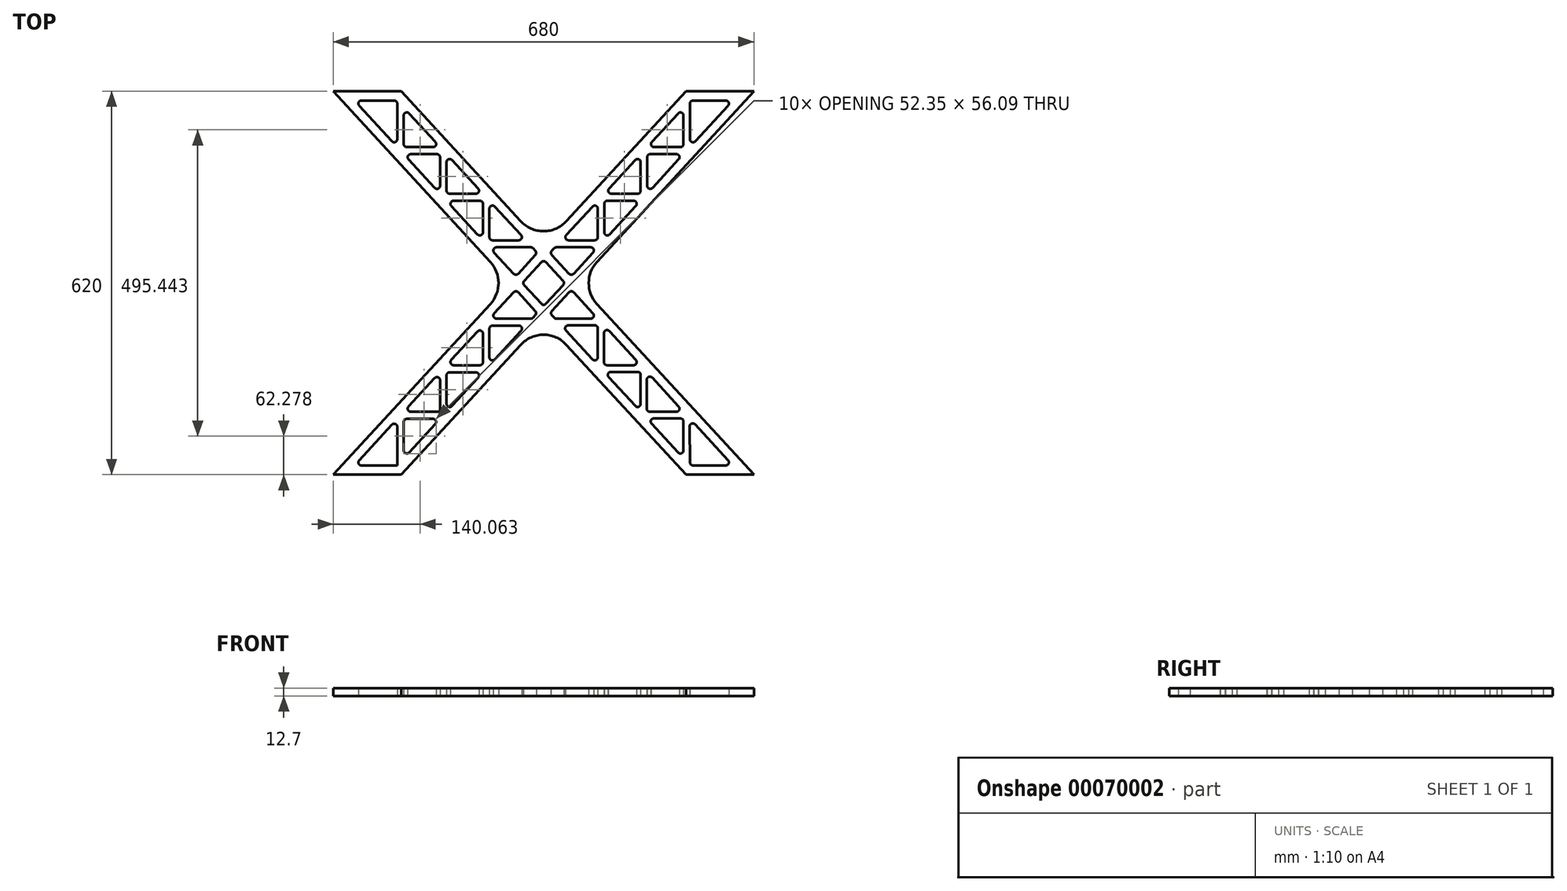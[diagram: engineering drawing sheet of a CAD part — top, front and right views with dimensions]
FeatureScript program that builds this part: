
annotation { "Feature Type Name" : "Feature", "Feature Type Description" : "" }
export const myFeature = defineFeature(function(context is Context, id is Id, definition is map)
    precondition{}
    {
        {
            var Q0;
            Q0=qCreatedBy(makeId("Top.planeOp"),FACE);
            var sketch = newSketch(context, id + "F0", { "sketchPlane" : qUnion([Q0])});
            skLineSegment(sketch, "E0.bottom", {"start": v(-340, 0) * mm, "end": v(-230, 0) * mm});
            skLineSegment(sketch, "E0.top", {"start": v(-340, 620) * mm, "end": v(-230, 620) * mm});
            skLineSegment(sketch, "E1", {"start": v(-230, 0) * mm, "end": v(-36.8, 210.14) * mm});
            skLineSegment(sketch, "E2", {"start": v(230, 620) * mm, "end": v(36.8, 409.86) * mm});
            skLineSegment(sketch, "E3", {"start": v(340, 0) * mm, "end": v(86.11, 276.16) * mm});
            skLineSegment(sketch, "E4", {"start": v(230, 0) * mm, "end": v(36.8, 210.14) * mm});
            skLineSegment(sketch, "E5.trimOffspring", {"start": v(230, 0) * mm, "end": v(340, 0) * mm});
            skLineSegment(sketch, "E6.trimOffspring", {"start": v(230, 620) * mm, "end": v(340, 620) * mm});
            skLineSegment(sketch, "E7.trimOffspring", {"start": v(-86.11, 343.84) * mm, "end": v(-340, 620) * mm});
            skLineSegment(sketch, "E8.trimOffspring", {"start": v(-86.11, 276.16) * mm, "end": v(-340, 0) * mm});
            skLineSegment(sketch, "E9.trimOffspring", {"start": v(-36.8, 409.86) * mm, "end": v(-230, 620) * mm});
            skLineSegment(sketch, "E10.trimOffspring", {"start": v(86.11, 343.84) * mm, "end": v(340, 620) * mm});
            skArc(sketch, "E11.filletArc", {"start": v(-36.8, 409.86) * mm, "mid": v(0, 393.7) * mm, "end": v(36.8, 409.86) * mm});
            skArc(sketch, "E12.filletArc", {"start": v(-86.11, 276.16) * mm, "mid": v(-72.92, 310) * mm, "end": v(-86.11, 343.84) * mm});
            skArc(sketch, "E13.filletArc", {"start": v(86.11, 343.84) * mm, "mid": v(72.92, 310) * mm, "end": v(86.11, 276.16) * mm});
            skArc(sketch, "E14.filletArc", {"start": v(36.8, 210.14) * mm, "mid": v(0, 226.3) * mm, "end": v(-36.8, 210.14) * mm});
            skLineSegment(sketch, "E15.0", {"start": v(-47.85, 399.7) * mm, "end": v(-78.93, 433.52) * mm});
            skLineSegment(sketch, "E15.1", {"start": v(-294.45, 605) * mm, "end": v(-241.59, 605) * mm});
            skLineSegment(sketch, "E15.2", {"start": v(-75.07, 354) * mm, "end": v(-79.9, 359.25) * mm});
            skLineSegment(sketch, "E15.4", {"start": v(-75.07, 266) * mm, "end": v(-79.9, 260.75) * mm});
            skLineSegment(sketch, "E15.6", {"start": v(75.07, 354) * mm, "end": v(79.9, 359.25) * mm});
            skLineSegment(sketch, "E15.7", {"start": v(241.59, 605) * mm, "end": v(294.45, 605) * mm});
            skLineSegment(sketch, "E15.8", {"start": v(217.43, 584.16) * mm, "end": v(175.04, 538.06) * mm});
            skLineSegment(sketch, "E15.9", {"start": v(298.13, 23.38) * mm, "end": v(244.76, 81.43) * mm});
            skLineSegment(sketch, "E15.10", {"start": v(241.55, 15) * mm, "end": v(294.45, 15) * mm});
            skLineSegment(sketch, "E15.11", {"start": v(217.43, 35.84) * mm, "end": v(174.44, 82.6) * mm});
            skLineSegment(sketch, "E15.13", {"start": v(-217.43, 35.84) * mm, "end": v(-175.04, 81.94) * mm});
            skLineSegment(sketch, "E15.15", {"start": v(-294.45, 15) * mm, "end": v(-236.59, 15) * mm});
            skLineSegment(sketch, "E16", {"start": v(-236.59, 15) * mm, "end": v(-236.59, 77.5) * mm});
            skLineSegment(sketch, "E17", {"start": v(-221.1, 90.32) * mm, "end": v(-178.73, 90.32) * mm});
            skLineSegment(sketch, "E18", {"start": v(-167.34, 101.72) * mm, "end": v(-167.34, 152.82) * mm});
            skLineSegment(sketch, "E19", {"start": v(-151.86, 165.65) * mm, "end": v(-109.48, 165.65) * mm});
            skLineSegment(sketch, "E20", {"start": v(-98.09, 182.04) * mm, "end": v(-98.09, 228.14) * mm});
            skLineSegment(sketch, "E21", {"start": v(-82.63, 241.02) * mm, "end": v(-40.07, 241.16) * mm});
            skLineSegment(sketch, "E22", {"start": v(97.48, 228.8) * mm, "end": v(97.48, 182.04) * mm});
            skLineSegment(sketch, "E23", {"start": v(108.87, 166.3) * mm, "end": v(151.86, 166.3) * mm});
            skLineSegment(sketch, "E24", {"start": v(166.73, 153.48) * mm, "end": v(166.73, 106.72) * mm});
            skLineSegment(sketch, "E25", {"start": v(178.12, 90.98) * mm, "end": v(221.1, 90.98) * mm});
            skLineSegment(sketch, "E26", {"start": v(236.08, 78) * mm, "end": v(236.55, 19.96) * mm});
            skLineSegment(sketch, "E27", {"start": v(-226.1, 39.22) * mm, "end": v(-226.1, 85.32) * mm});
            skLineSegment(sketch, "E28", {"start": v(-214.72, 101.72) * mm, "end": v(-167.34, 101.72) * mm});
            skLineSegment(sketch, "E29", {"start": v(-156.86, 114.54) * mm, "end": v(-156.86, 160.65) * mm});
            skLineSegment(sketch, "E30", {"start": v(-145.47, 177.04) * mm, "end": v(-103.09, 177.04) * mm});
            skLineSegment(sketch, "E31", {"start": v(-87.61, 189.87) * mm, "end": v(-87.61, 236.02) * mm});
            skLineSegment(sketch, "E32", {"start": v(-76.22, 252.36) * mm, "end": v(-20.56, 252.36) * mm});
            skLineSegment(sketch, "E33", {"start": v(87.61, 236.58) * mm, "end": v(87.61, 189.87) * mm});
            skLineSegment(sketch, "E34", {"start": v(102.48, 177.04) * mm, "end": v(145.47, 177.04) * mm});
            skLineSegment(sketch, "E35", {"start": v(156.86, 161.3) * mm, "end": v(156.86, 114.54) * mm});
            skLineSegment(sketch, "E36", {"start": v(171.73, 101.72) * mm, "end": v(214.5, 101.72) * mm});
            skLineSegment(sketch, "E37", {"start": v(226.1, 85.98) * mm, "end": v(226.1, 39.22) * mm});
            skLineSegment(sketch, "E38", {"start": v(-236.59, 600) * mm, "end": v(-236.59, 542.5) * mm});
            skLineSegment(sketch, "E39", {"start": v(-221.1, 529.68) * mm, "end": v(-178.73, 529.68) * mm});
            skLineSegment(sketch, "E40", {"start": v(-167.34, 513.28) * mm, "end": v(-167.34, 467.18) * mm});
            skLineSegment(sketch, "E41", {"start": v(-151.86, 454.35) * mm, "end": v(-109.48, 454.35) * mm});
            skLineSegment(sketch, "E42", {"start": v(-98.09, 437.96) * mm, "end": v(-98.09, 391.86) * mm});
            skLineSegment(sketch, "E43", {"start": v(-82.61, 379.03) * mm, "end": v(-40.23, 379.03) * mm});
            skLineSegment(sketch, "E44", {"start": v(98.09, 391.86) * mm, "end": v(98.09, 437.96) * mm});
            skLineSegment(sketch, "E45", {"start": v(109.48, 454.35) * mm, "end": v(151.86, 454.35) * mm});
            skLineSegment(sketch, "E46", {"start": v(167.34, 467.18) * mm, "end": v(167.34, 513.28) * mm});
            skLineSegment(sketch, "E47", {"start": v(178.73, 529.68) * mm, "end": v(221.1, 529.68) * mm});
            skLineSegment(sketch, "E48", {"start": v(236.59, 542.5) * mm, "end": v(236.59, 600) * mm});
            skLineSegment(sketch, "E49", {"start": v(226.1, 580.78) * mm, "end": v(226.1, 534.68) * mm});
            skLineSegment(sketch, "E50", {"start": v(214.72, 518.28) * mm, "end": v(172.34, 518.28) * mm});
            skLineSegment(sketch, "E51", {"start": v(156.86, 505.46) * mm, "end": v(156.86, 459.35) * mm});
            skLineSegment(sketch, "E52", {"start": v(145.47, 442.96) * mm, "end": v(103.09, 442.96) * mm});
            skLineSegment(sketch, "E53", {"start": v(87.61, 430.13) * mm, "end": v(87.61, 384.03) * mm});
            skLineSegment(sketch, "E54", {"start": v(76.22, 367.64) * mm, "end": v(20.56, 367.64) * mm});
            skLineSegment(sketch, "E55", {"start": v(-87.61, 384.03) * mm, "end": v(-87.61, 430.13) * mm});
            skLineSegment(sketch, "E56", {"start": v(-103.09, 442.96) * mm, "end": v(-145.47, 442.96) * mm});
            skLineSegment(sketch, "E57", {"start": v(-156.86, 459.35) * mm, "end": v(-156.86, 505.46) * mm});
            skLineSegment(sketch, "E58", {"start": v(-172.34, 518.28) * mm, "end": v(-214.72, 518.28) * mm});
            skLineSegment(sketch, "E59", {"start": v(-226.1, 534.68) * mm, "end": v(-226.1, 580.78) * mm});
            skLineSegment(sketch, "E60", {"start": v(47.85, 220.3) * mm, "end": v(36.12, 233.05) * mm});
            skLineSegment(sketch, "E61", {"start": v(-41.13, 294.91) * mm, "end": v(-13.3, 264.64) * mm});
            skLineSegment(sketch, "E62", {"start": v(75.07, 354) * mm, "end": v(48.5, 325.09) * mm});
            skLineSegment(sketch, "E63", {"start": v(-75.07, 266) * mm, "end": v(-48.5, 294.91) * mm});
            skLineSegment(sketch, "E64", {"start": v(75.07, 266) * mm, "end": v(48.5, 294.91) * mm});
            skLineSegment(sketch, "E65.trimOffspring", {"start": v(-245.27, 539.12) * mm, "end": v(-298.13, 596.62) * mm});
            skLineSegment(sketch, "E66.trimOffspring", {"start": v(-175.04, 538.06) * mm, "end": v(-217.43, 584.16) * mm});
            skLineSegment(sketch, "E67.trimOffspring", {"start": v(-176.02, 463.8) * mm, "end": v(-218.4, 509.9) * mm});
            skLineSegment(sketch, "E68.trimOffspring", {"start": v(-105.8, 462.74) * mm, "end": v(-148.18, 508.84) * mm});
            skLineSegment(sketch, "E69.trimOffspring", {"start": v(-106.77, 388.47) * mm, "end": v(-149.15, 434.58) * mm});
            skLineSegment(sketch, "E70.trimOffspring", {"start": v(-31.51, 313.38) * mm, "end": v(-3.68, 343.66) * mm});
            skLineSegment(sketch, "E71.trimOffspring", {"start": v(-48.5, 325.09) * mm, "end": v(-75.07, 354) * mm});
            skLineSegment(sketch, "E72.trimOffspring", {"start": v(40.23, 379.03) * mm, "end": v(82.61, 379.03) * mm});
            skLineSegment(sketch, "E73.trimOffspring", {"start": v(13.3, 355.36) * mm, "end": v(41.13, 325.09) * mm});
            skLineSegment(sketch, "E74.trimOffspring", {"start": v(-13.3, 362.13) * mm, "end": v(-16.88, 366.02) * mm});
            skLineSegment(sketch, "E75.trimOffspring", {"start": v(-20.56, 367.64) * mm, "end": v(-76.22, 367.64) * mm});
            skLineSegment(sketch, "E76.trimOffspring", {"start": v(-13.3, 355.36) * mm, "end": v(-41.13, 325.09) * mm});
            skLineSegment(sketch, "E77.trimOffspring", {"start": v(-36.55, 387.42) * mm, "end": v(-47.85, 399.7) * mm});
            skLineSegment(sketch, "E78.trimOffspring", {"start": v(36.55, 387.42) * mm, "end": v(47.85, 399.7) * mm});
            skLineSegment(sketch, "E79.trimOffspring", {"start": v(78.93, 433.52) * mm, "end": v(47.85, 399.7) * mm});
            skLineSegment(sketch, "E80.trimOffspring", {"start": v(176.02, 463.8) * mm, "end": v(218.4, 509.9) * mm});
            skLineSegment(sketch, "E81.trimOffspring", {"start": v(148.18, 508.84) * mm, "end": v(105.8, 462.74) * mm});
            skLineSegment(sketch, "E82.trimOffspring", {"start": v(245.27, 539.12) * mm, "end": v(298.13, 596.62) * mm});
            skLineSegment(sketch, "E83.trimOffspring", {"start": v(106.77, 388.47) * mm, "end": v(149.15, 434.58) * mm});
            skLineSegment(sketch, "E84.trimOffspring", {"start": v(13.3, 362.13) * mm, "end": v(16.88, 366.02) * mm});
            skLineSegment(sketch, "E85.trimOffspring", {"start": v(31.51, 306.62) * mm, "end": v(3.68, 276.34) * mm});
            skLineSegment(sketch, "E86.trimOffspring", {"start": v(31.51, 313.38) * mm, "end": v(3.68, 343.66) * mm});
            skLineSegment(sketch, "E87.trimOffspring", {"start": v(-13.3, 257.87) * mm, "end": v(-16.88, 253.98) * mm});
            skLineSegment(sketch, "E88.trimOffspring", {"start": v(-3.68, 276.34) * mm, "end": v(-31.51, 306.62) * mm});
            skLineSegment(sketch, "E89.trimOffspring", {"start": v(13.3, 264.64) * mm, "end": v(41.13, 294.91) * mm});
            skLineSegment(sketch, "E90.trimOffspring", {"start": v(20.56, 252.36) * mm, "end": v(76.22, 252.36) * mm});
            skLineSegment(sketch, "E91.trimOffspring", {"start": v(39.79, 241.43) * mm, "end": v(82.6, 241.58) * mm});
            skLineSegment(sketch, "E92.trimOffspring", {"start": v(16.88, 253.98) * mm, "end": v(13.3, 257.87) * mm});
            skLineSegment(sketch, "E93.trimOffspring", {"start": v(79.9, 260.75) * mm, "end": v(75.07, 266) * mm});
            skLineSegment(sketch, "E94.trimOffspring", {"start": v(78.93, 186.48) * mm, "end": v(47.85, 220.3) * mm});
            skLineSegment(sketch, "E95.trimOffspring", {"start": v(-36.37, 232.78) * mm, "end": v(-47.85, 220.3) * mm});
            skLineSegment(sketch, "E96.trimOffspring", {"start": v(-106.77, 231.53) * mm, "end": v(-149.15, 185.42) * mm});
            skLineSegment(sketch, "E97.trimOffspring", {"start": v(-78.93, 186.48) * mm, "end": v(-47.85, 220.3) * mm});
            skLineSegment(sketch, "E98.trimOffspring", {"start": v(-176.02, 156.2) * mm, "end": v(-218.4, 110.1) * mm});
            skLineSegment(sketch, "E99.trimOffspring", {"start": v(-148.18, 111.16) * mm, "end": v(-105.8, 157.26) * mm});
            skLineSegment(sketch, "E100.trimOffspring", {"start": v(-245.27, 80.88) * mm, "end": v(-298.13, 23.38) * mm});
            skLineSegment(sketch, "E101.trimOffspring", {"start": v(218.25, 110.27) * mm, "end": v(175.41, 156.86) * mm});
            skLineSegment(sketch, "E102.trimOffspring", {"start": v(148.18, 111.16) * mm, "end": v(105.2, 157.92) * mm});
            skLineSegment(sketch, "E103.trimOffspring", {"start": v(149.15, 185.42) * mm, "end": v(106.16, 232.18) * mm});
            skPoint(sketch, "E104.visualSharp", {"position": v(-305.83, 605) * mm});
            skArc(sketch, "E104.filletArc", {"start": v(-294.45, 605) * mm, "mid": v(-299.02, 602) * mm, "end": v(-298.13, 596.62) * mm});
            skPoint(sketch, "E105.visualSharp", {"position": v(-236.59, 605) * mm});
            skArc(sketch, "E105.filletArc", {"start": v(-236.59, 600) * mm, "mid": v(-238.05, 603.54) * mm, "end": v(-241.59, 605) * mm});
            skPoint(sketch, "E106.visualSharp", {"position": v(-236.59, 529.68) * mm});
            skArc(sketch, "E106.filletArc", {"start": v(-245.27, 539.12) * mm, "mid": v(-239.77, 537.84) * mm, "end": v(-236.59, 542.5) * mm});
            skPoint(sketch, "E107.visualSharp", {"position": v(-226.1, 593.6) * mm});
            skArc(sketch, "E107.filletArc", {"start": v(-217.43, 584.16) * mm, "mid": v(-222.93, 585.44) * mm, "end": v(-226.1, 580.78) * mm});
            skPoint(sketch, "E108.visualSharp", {"position": v(-167.34, 529.68) * mm});
            skArc(sketch, "E108.filletArc", {"start": v(-178.73, 529.68) * mm, "mid": v(-174.15, 532.67) * mm, "end": v(-175.04, 538.06) * mm});
            skPoint(sketch, "E109.visualSharp", {"position": v(-226.1, 529.68) * mm});
            skArc(sketch, "E109.filletArc", {"start": v(-226.1, 534.68) * mm, "mid": v(-224.65, 531.14) * mm, "end": v(-221.1, 529.68) * mm});
            skPoint(sketch, "E110.visualSharp", {"position": v(-156.86, 518.28) * mm});
            skArc(sketch, "E110.filletArc", {"start": v(-148.18, 508.84) * mm, "mid": v(-153.68, 510.11) * mm, "end": v(-156.86, 505.46) * mm});
            skPoint(sketch, "E111.visualSharp", {"position": v(-98.09, 454.35) * mm});
            skArc(sketch, "E111.filletArc", {"start": v(-109.48, 454.35) * mm, "mid": v(-104.9, 457.34) * mm, "end": v(-105.8, 462.74) * mm});
            skPoint(sketch, "E112.visualSharp", {"position": v(-156.86, 454.35) * mm});
            skArc(sketch, "E112.filletArc", {"start": v(-156.86, 459.35) * mm, "mid": v(-155.4, 455.82) * mm, "end": v(-151.86, 454.35) * mm});
            skPoint(sketch, "E113.visualSharp", {"position": v(-167.34, 454.35) * mm});
            skArc(sketch, "E113.filletArc", {"start": v(-176.02, 463.8) * mm, "mid": v(-170.52, 462.52) * mm, "end": v(-167.34, 467.18) * mm});
            skPoint(sketch, "E114.visualSharp", {"position": v(-167.34, 518.28) * mm});
            skArc(sketch, "E114.filletArc", {"start": v(-167.34, 513.28) * mm, "mid": v(-168.8, 516.82) * mm, "end": v(-172.34, 518.28) * mm});
            skPoint(sketch, "E115.visualSharp", {"position": v(-226.1, 518.28) * mm});
            skArc(sketch, "E115.filletArc", {"start": v(-214.72, 518.28) * mm, "mid": v(-219.3, 515.3) * mm, "end": v(-218.4, 509.9) * mm});
            skPoint(sketch, "E116.visualSharp", {"position": v(-98.09, 442.96) * mm});
            skArc(sketch, "E116.filletArc", {"start": v(-98.09, 437.96) * mm, "mid": v(-99.55, 441.5) * mm, "end": v(-103.09, 442.96) * mm});
            skPoint(sketch, "E117.visualSharp", {"position": v(-98.09, 379.03) * mm});
            skArc(sketch, "E117.filletArc", {"start": v(-106.77, 388.47) * mm, "mid": v(-101.27, 387.2) * mm, "end": v(-98.09, 391.86) * mm});
            skPoint(sketch, "E118.visualSharp", {"position": v(-156.86, 442.96) * mm});
            skArc(sketch, "E118.filletArc", {"start": v(-145.47, 442.96) * mm, "mid": v(-150.05, 439.97) * mm, "end": v(-149.15, 434.58) * mm});
            skPoint(sketch, "E119.visualSharp", {"position": v(-87.61, 442.96) * mm});
            skArc(sketch, "E119.filletArc", {"start": v(-78.93, 433.52) * mm, "mid": v(-84.43, 434.8) * mm, "end": v(-87.61, 430.13) * mm});
            skPoint(sketch, "E120.visualSharp", {"position": v(-28.84, 379.03) * mm});
            skArc(sketch, "E120.filletArc", {"start": v(-40.23, 379.03) * mm, "mid": v(-35.65, 382.02) * mm, "end": v(-36.55, 387.42) * mm});
            skPoint(sketch, "E121.visualSharp", {"position": v(-87.61, 379.03) * mm});
            skArc(sketch, "E121.filletArc", {"start": v(-87.61, 384.03) * mm, "mid": v(-86.15, 380.5) * mm, "end": v(-82.61, 379.03) * mm});
            skPoint(sketch, "E122.visualSharp", {"position": v(28.84, 379.03) * mm});
            skArc(sketch, "E122.filletArc", {"start": v(36.55, 387.42) * mm, "mid": v(35.65, 382.02) * mm, "end": v(40.23, 379.03) * mm});
            skPoint(sketch, "E123.visualSharp", {"position": v(87.61, 379.03) * mm});
            skArc(sketch, "E123.filletArc", {"start": v(82.61, 379.03) * mm, "mid": v(86.15, 380.5) * mm, "end": v(87.61, 384.03) * mm});
            skPoint(sketch, "E124.visualSharp", {"position": v(87.61, 442.96) * mm});
            skArc(sketch, "E124.filletArc", {"start": v(87.61, 430.13) * mm, "mid": v(84.43, 434.8) * mm, "end": v(78.93, 433.52) * mm});
            skPoint(sketch, "E125.visualSharp", {"position": v(98.09, 442.96) * mm});
            skArc(sketch, "E125.filletArc", {"start": v(103.09, 442.96) * mm, "mid": v(99.55, 441.5) * mm, "end": v(98.09, 437.96) * mm});
            skPoint(sketch, "E126.visualSharp", {"position": v(98.09, 379.03) * mm});
            skArc(sketch, "E126.filletArc", {"start": v(98.09, 391.86) * mm, "mid": v(101.27, 387.2) * mm, "end": v(106.77, 388.47) * mm});
            skPoint(sketch, "E127.visualSharp", {"position": v(156.86, 442.96) * mm});
            skArc(sketch, "E127.filletArc", {"start": v(149.15, 434.58) * mm, "mid": v(150.05, 439.97) * mm, "end": v(145.47, 442.96) * mm});
            skPoint(sketch, "E128.visualSharp", {"position": v(167.34, 454.35) * mm});
            skArc(sketch, "E128.filletArc", {"start": v(167.34, 467.18) * mm, "mid": v(170.52, 462.52) * mm, "end": v(176.02, 463.8) * mm});
            skPoint(sketch, "E129.visualSharp", {"position": v(226.1, 518.28) * mm});
            skArc(sketch, "E129.filletArc", {"start": v(218.4, 509.9) * mm, "mid": v(219.3, 515.3) * mm, "end": v(214.72, 518.28) * mm});
            skPoint(sketch, "E130.visualSharp", {"position": v(167.34, 518.28) * mm});
            skArc(sketch, "E130.filletArc", {"start": v(172.34, 518.28) * mm, "mid": v(168.8, 516.82) * mm, "end": v(167.34, 513.28) * mm});
            skPoint(sketch, "E131.visualSharp", {"position": v(156.86, 518.28) * mm});
            skArc(sketch, "E131.filletArc", {"start": v(156.86, 505.46) * mm, "mid": v(153.68, 510.11) * mm, "end": v(148.18, 508.84) * mm});
            skPoint(sketch, "E132.visualSharp", {"position": v(156.86, 454.35) * mm});
            skArc(sketch, "E132.filletArc", {"start": v(151.86, 454.35) * mm, "mid": v(155.4, 455.82) * mm, "end": v(156.86, 459.35) * mm});
            skPoint(sketch, "E133.visualSharp", {"position": v(98.09, 454.35) * mm});
            skArc(sketch, "E133.filletArc", {"start": v(105.8, 462.74) * mm, "mid": v(104.9, 457.34) * mm, "end": v(109.48, 454.35) * mm});
            skPoint(sketch, "E134.visualSharp", {"position": v(167.34, 529.68) * mm});
            skArc(sketch, "E134.filletArc", {"start": v(175.04, 538.06) * mm, "mid": v(174.15, 532.67) * mm, "end": v(178.73, 529.68) * mm});
            skPoint(sketch, "E135.visualSharp", {"position": v(226.1, 529.68) * mm});
            skArc(sketch, "E135.filletArc", {"start": v(221.1, 529.68) * mm, "mid": v(224.65, 531.14) * mm, "end": v(226.1, 534.68) * mm});
            skPoint(sketch, "E136.visualSharp", {"position": v(226.1, 593.6) * mm});
            skArc(sketch, "E136.filletArc", {"start": v(226.1, 580.78) * mm, "mid": v(222.93, 585.44) * mm, "end": v(217.43, 584.16) * mm});
            skPoint(sketch, "E137.visualSharp", {"position": v(236.59, 605) * mm});
            skArc(sketch, "E137.filletArc", {"start": v(241.59, 605) * mm, "mid": v(238.05, 603.54) * mm, "end": v(236.59, 600) * mm});
            skPoint(sketch, "E138.visualSharp", {"position": v(236.59, 529.68) * mm});
            skArc(sketch, "E138.filletArc", {"start": v(236.59, 542.5) * mm, "mid": v(239.77, 537.84) * mm, "end": v(245.27, 539.12) * mm});
            skPoint(sketch, "E139.visualSharp", {"position": v(305.83, 605) * mm});
            skArc(sketch, "E139.filletArc", {"start": v(298.13, 596.62) * mm, "mid": v(299.02, 602) * mm, "end": v(294.45, 605) * mm});
            skPoint(sketch, "E140.visualSharp", {"position": v(18.36, 367.64) * mm});
            skArc(sketch, "E140.filletArc", {"start": v(20.56, 367.64) * mm, "mid": v(18.55, 367.21) * mm, "end": v(16.88, 366.02) * mm});
            skPoint(sketch, "E141.visualSharp", {"position": v(10.19, 358.74) * mm});
            skArc(sketch, "E141.filletArc", {"start": v(13.3, 362.13) * mm, "mid": v(11.98, 358.74) * mm, "end": v(13.3, 355.36) * mm});
            skPoint(sketch, "E142.visualSharp", {"position": v(44.81, 321.08) * mm});
            skArc(sketch, "E142.filletArc", {"start": v(41.13, 325.09) * mm, "mid": v(44.81, 323.47) * mm, "end": v(48.5, 325.09) * mm});
            skPoint(sketch, "E143.visualSharp", {"position": v(87.61, 367.64) * mm});
            skArc(sketch, "E143.filletArc", {"start": v(79.9, 359.25) * mm, "mid": v(80.8, 364.65) * mm, "end": v(76.22, 367.64) * mm});
            skPoint(sketch, "E144.visualSharp", {"position": v(-10.19, 358.74) * mm});
            skArc(sketch, "E144.filletArc", {"start": v(-13.3, 355.36) * mm, "mid": v(-11.98, 358.74) * mm, "end": v(-13.3, 362.13) * mm});
            skPoint(sketch, "E145.visualSharp", {"position": v(-18.36, 367.64) * mm});
            skArc(sketch, "E145.filletArc", {"start": v(-16.88, 366.02) * mm, "mid": v(-18.55, 367.21) * mm, "end": v(-20.56, 367.64) * mm});
            skPoint(sketch, "E146.visualSharp", {"position": v(-44.81, 321.08) * mm});
            skArc(sketch, "E146.filletArc", {"start": v(-48.5, 325.09) * mm, "mid": v(-44.81, 323.47) * mm, "end": v(-41.13, 325.09) * mm});
            skPoint(sketch, "E147.visualSharp", {"position": v(-87.61, 367.64) * mm});
            skArc(sketch, "E147.filletArc", {"start": v(-76.22, 367.64) * mm, "mid": v(-80.8, 364.65) * mm, "end": v(-79.9, 359.25) * mm});
            skPoint(sketch, "E148.visualSharp", {"position": v(0, 347.66) * mm});
            skArc(sketch, "E148.filletArc", {"start": v(3.68, 343.66) * mm, "mid": v(0, 345.27) * mm, "end": v(-3.68, 343.66) * mm});
            skPoint(sketch, "E149.visualSharp", {"position": v(-34.62, 310) * mm});
            skArc(sketch, "E149.filletArc", {"start": v(-31.51, 313.38) * mm, "mid": v(-32.83, 310) * mm, "end": v(-31.51, 306.62) * mm});
            skPoint(sketch, "E150.visualSharp", {"position": v(34.62, 310) * mm});
            skArc(sketch, "E150.filletArc", {"start": v(31.51, 306.62) * mm, "mid": v(32.83, 310) * mm, "end": v(31.51, 313.38) * mm});
            skPoint(sketch, "E151.visualSharp", {"position": v(0, 272.34) * mm});
            skArc(sketch, "E151.filletArc", {"start": v(-3.68, 276.34) * mm, "mid": v(0, 274.73) * mm, "end": v(3.68, 276.34) * mm});
            skPoint(sketch, "E152.visualSharp", {"position": v(-10.19, 261.26) * mm});
            skArc(sketch, "E152.filletArc", {"start": v(-13.3, 257.87) * mm, "mid": v(-11.98, 261.26) * mm, "end": v(-13.3, 264.64) * mm});
            skPoint(sketch, "E153.visualSharp", {"position": v(-44.81, 298.92) * mm});
            skArc(sketch, "E153.filletArc", {"start": v(-41.13, 294.91) * mm, "mid": v(-44.81, 296.53) * mm, "end": v(-48.5, 294.91) * mm});
            skPoint(sketch, "E154.visualSharp", {"position": v(-87.61, 252.36) * mm});
            skArc(sketch, "E154.filletArc", {"start": v(-79.9, 260.75) * mm, "mid": v(-80.8, 255.35) * mm, "end": v(-76.22, 252.36) * mm});
            skPoint(sketch, "E155.visualSharp", {"position": v(-87.61, 241) * mm});
            skArc(sketch, "E155.filletArc", {"start": v(-82.63, 241.02) * mm, "mid": v(-86.15, 239.55) * mm, "end": v(-87.61, 236.02) * mm});
            skPoint(sketch, "E156.visualSharp", {"position": v(-28.63, 241.2) * mm});
            skArc(sketch, "E156.filletArc", {"start": v(-36.37, 232.78) * mm, "mid": v(-35.47, 238.18) * mm, "end": v(-40.07, 241.16) * mm});
            skPoint(sketch, "E157.visualSharp", {"position": v(-87.61, 177.04) * mm});
            skArc(sketch, "E157.filletArc", {"start": v(-87.61, 189.87) * mm, "mid": v(-84.43, 185.2) * mm, "end": v(-78.93, 186.48) * mm});
            skPoint(sketch, "E158.visualSharp", {"position": v(-98.09, 177.04) * mm});
            skArc(sketch, "E158.filletArc", {"start": v(-103.09, 177.04) * mm, "mid": v(-99.55, 178.5) * mm, "end": v(-98.09, 182.04) * mm});
            skPoint(sketch, "E159.visualSharp", {"position": v(-98.09, 240.97) * mm});
            skArc(sketch, "E159.filletArc", {"start": v(-98.09, 228.14) * mm, "mid": v(-101.27, 232.8) * mm, "end": v(-106.77, 231.53) * mm});
            skPoint(sketch, "E160.visualSharp", {"position": v(-156.86, 177.04) * mm});
            skArc(sketch, "E160.filletArc", {"start": v(-149.15, 185.42) * mm, "mid": v(-150.05, 180.03) * mm, "end": v(-145.47, 177.04) * mm});
            skPoint(sketch, "E161.visualSharp", {"position": v(-98.09, 165.65) * mm});
            skArc(sketch, "E161.filletArc", {"start": v(-105.8, 157.26) * mm, "mid": v(-104.9, 162.66) * mm, "end": v(-109.48, 165.65) * mm});
            skPoint(sketch, "E162.visualSharp", {"position": v(-156.86, 165.65) * mm});
            skArc(sketch, "E162.filletArc", {"start": v(-151.86, 165.65) * mm, "mid": v(-155.4, 164.18) * mm, "end": v(-156.86, 160.65) * mm});
            skPoint(sketch, "E163.visualSharp", {"position": v(-156.86, 101.72) * mm});
            skArc(sketch, "E163.filletArc", {"start": v(-156.86, 114.54) * mm, "mid": v(-153.68, 109.89) * mm, "end": v(-148.18, 111.16) * mm});
            skPoint(sketch, "E164.visualSharp", {"position": v(-167.34, 165.65) * mm});
            skArc(sketch, "E164.filletArc", {"start": v(-167.34, 152.82) * mm, "mid": v(-170.52, 157.48) * mm, "end": v(-176.02, 156.2) * mm});
            skPoint(sketch, "E165.visualSharp", {"position": v(-226.1, 101.72) * mm});
            skArc(sketch, "E165.filletArc", {"start": v(-218.4, 110.1) * mm, "mid": v(-219.3, 104.7) * mm, "end": v(-214.72, 101.72) * mm});
            skPoint(sketch, "E166.visualSharp", {"position": v(-226.1, 26.4) * mm});
            skArc(sketch, "E166.filletArc", {"start": v(-226.1, 39.22) * mm, "mid": v(-222.93, 34.56) * mm, "end": v(-217.43, 35.84) * mm});
            skPoint(sketch, "E167.visualSharp", {"position": v(-167.34, 90.32) * mm});
            skArc(sketch, "E167.filletArc", {"start": v(-175.04, 81.94) * mm, "mid": v(-174.15, 87.33) * mm, "end": v(-178.73, 90.32) * mm});
            skPoint(sketch, "E168.visualSharp", {"position": v(-236.59, 90.32) * mm});
            skArc(sketch, "E168.filletArc", {"start": v(-236.59, 77.5) * mm, "mid": v(-239.77, 82.16) * mm, "end": v(-245.27, 80.88) * mm});
            skPoint(sketch, "E169.visualSharp", {"position": v(-305.83, 15) * mm});
            skArc(sketch, "E169.filletArc", {"start": v(-298.13, 23.38) * mm, "mid": v(-299.02, 18) * mm, "end": v(-294.45, 15) * mm});
            skPoint(sketch, "E170.visualSharp", {"position": v(-226.1, 90.32) * mm});
            skArc(sketch, "E170.filletArc", {"start": v(-221.1, 90.32) * mm, "mid": v(-224.65, 88.86) * mm, "end": v(-226.1, 85.32) * mm});
            skPoint(sketch, "E171.visualSharp", {"position": v(44.81, 298.92) * mm});
            skArc(sketch, "E171.filletArc", {"start": v(48.5, 294.91) * mm, "mid": v(44.81, 296.53) * mm, "end": v(41.13, 294.91) * mm});
            skPoint(sketch, "E172.visualSharp", {"position": v(10.19, 261.26) * mm});
            skArc(sketch, "E172.filletArc", {"start": v(13.3, 264.64) * mm, "mid": v(11.98, 261.26) * mm, "end": v(13.3, 257.87) * mm});
            skPoint(sketch, "E173.visualSharp", {"position": v(87.61, 252.36) * mm});
            skArc(sketch, "E173.filletArc", {"start": v(76.22, 252.36) * mm, "mid": v(80.8, 255.35) * mm, "end": v(79.9, 260.75) * mm});
            skPoint(sketch, "E174.visualSharp", {"position": v(18.36, 252.36) * mm});
            skArc(sketch, "E174.filletArc", {"start": v(16.88, 253.98) * mm, "mid": v(18.55, 252.79) * mm, "end": v(20.56, 252.36) * mm});
            skPoint(sketch, "E175.visualSharp", {"position": v(-18.36, 252.36) * mm});
            skArc(sketch, "E175.filletArc", {"start": v(-20.56, 252.36) * mm, "mid": v(-18.55, 252.79) * mm, "end": v(-16.88, 253.98) * mm});
            skPoint(sketch, "E176.visualSharp", {"position": v(28.45, 241.4) * mm});
            skArc(sketch, "E176.filletArc", {"start": v(39.79, 241.43) * mm, "mid": v(35.22, 238.43) * mm, "end": v(36.12, 233.05) * mm});
            skPoint(sketch, "E177.visualSharp", {"position": v(87.61, 241.6) * mm});
            skArc(sketch, "E177.filletArc", {"start": v(87.61, 236.58) * mm, "mid": v(86.14, 240.12) * mm, "end": v(82.6, 241.58) * mm});
            skPoint(sketch, "E178.visualSharp", {"position": v(87.61, 177.04) * mm});
            skArc(sketch, "E178.filletArc", {"start": v(78.93, 186.48) * mm, "mid": v(84.43, 185.2) * mm, "end": v(87.61, 189.87) * mm});
            skPoint(sketch, "E179.visualSharp", {"position": v(156.86, 177.04) * mm});
            skArc(sketch, "E179.filletArc", {"start": v(145.47, 177.04) * mm, "mid": v(150.05, 180.03) * mm, "end": v(149.15, 185.42) * mm});
            skPoint(sketch, "E180.visualSharp", {"position": v(97.48, 241.63) * mm});
            skArc(sketch, "E180.filletArc", {"start": v(106.16, 232.18) * mm, "mid": v(100.67, 233.46) * mm, "end": v(97.48, 228.8) * mm});
            skPoint(sketch, "E181.visualSharp", {"position": v(97.48, 177.04) * mm});
            skArc(sketch, "E181.filletArc", {"start": v(97.48, 182.04) * mm, "mid": v(98.95, 178.5) * mm, "end": v(102.48, 177.04) * mm});
            skPoint(sketch, "E182.visualSharp", {"position": v(97.48, 166.3) * mm});
            skArc(sketch, "E182.filletArc", {"start": v(108.87, 166.3) * mm, "mid": v(104.3, 163.31) * mm, "end": v(105.2, 157.92) * mm});
            skPoint(sketch, "E183.visualSharp", {"position": v(156.86, 166.3) * mm});
            skArc(sketch, "E183.filletArc", {"start": v(156.86, 161.3) * mm, "mid": v(155.4, 164.84) * mm, "end": v(151.86, 166.3) * mm});
            skPoint(sketch, "E184.visualSharp", {"position": v(156.86, 101.72) * mm});
            skArc(sketch, "E184.filletArc", {"start": v(148.18, 111.16) * mm, "mid": v(153.68, 109.89) * mm, "end": v(156.86, 114.54) * mm});
            skPoint(sketch, "E185.visualSharp", {"position": v(166.73, 166.3) * mm});
            skArc(sketch, "E185.filletArc", {"start": v(175.41, 156.86) * mm, "mid": v(169.92, 158.14) * mm, "end": v(166.73, 153.48) * mm});
            skPoint(sketch, "E186.visualSharp", {"position": v(166.73, 101.72) * mm});
            skArc(sketch, "E186.filletArc", {"start": v(166.73, 106.72) * mm, "mid": v(168.2, 103.18) * mm, "end": v(171.73, 101.72) * mm});
            skPoint(sketch, "E187.visualSharp", {"position": v(226.1, 101.72) * mm});
            skArc(sketch, "E187.filletArc", {"start": v(214.5, 101.72) * mm, "mid": v(219.16, 104.77) * mm, "end": v(218.25, 110.27) * mm});
            skPoint(sketch, "E188.visualSharp", {"position": v(226.1, 90.98) * mm});
            skArc(sketch, "E188.filletArc", {"start": v(226.1, 85.98) * mm, "mid": v(224.65, 89.52) * mm, "end": v(221.1, 90.98) * mm});
            skPoint(sketch, "E189.visualSharp", {"position": v(166.73, 90.98) * mm});
            skArc(sketch, "E189.filletArc", {"start": v(178.12, 90.98) * mm, "mid": v(173.54, 88) * mm, "end": v(174.44, 82.6) * mm});
            skPoint(sketch, "E190.visualSharp", {"position": v(226.1, 26.4) * mm});
            skArc(sketch, "E190.filletArc", {"start": v(217.43, 35.84) * mm, "mid": v(222.93, 34.56) * mm, "end": v(226.1, 39.22) * mm});
            skPoint(sketch, "E191.visualSharp", {"position": v(235.98, 90.98) * mm});
            skArc(sketch, "E191.filletArc", {"start": v(244.76, 81.43) * mm, "mid": v(239.25, 82.7) * mm, "end": v(236.08, 78) * mm});
            skPoint(sketch, "E192.visualSharp", {"position": v(236.59, 15) * mm});
            skArc(sketch, "E192.filletArc", {"start": v(236.55, 19.96) * mm, "mid": v(238.02, 16.45) * mm, "end": v(241.55, 15) * mm});
            skPoint(sketch, "E193.visualSharp", {"position": v(305.83, 15) * mm});
            skArc(sketch, "E193.filletArc", {"start": v(294.45, 15) * mm, "mid": v(299.02, 18) * mm, "end": v(298.13, 23.38) * mm});
            skSolve(sketch);
        }
        {
            var Q0;
            Q0 = qSketchRegion(id + "F0", true);
            var Q1;
            Q1=makeQuery(id+"F0.imprint","IMPRINT",FACE,{"disambiguationData":[TD([[makeQuery(id+"F0.imprint","IMPRINT",EDGE,{"derivedFrom":sQuery(id+"F0.wireOp",EDGE,"E0.bottom")}),1.0]])]});
            extrude(context, id + "F1", {"entities" : qUnion([Q0, Q1]), "depth" : 12.7 * mm});
        }
    });
